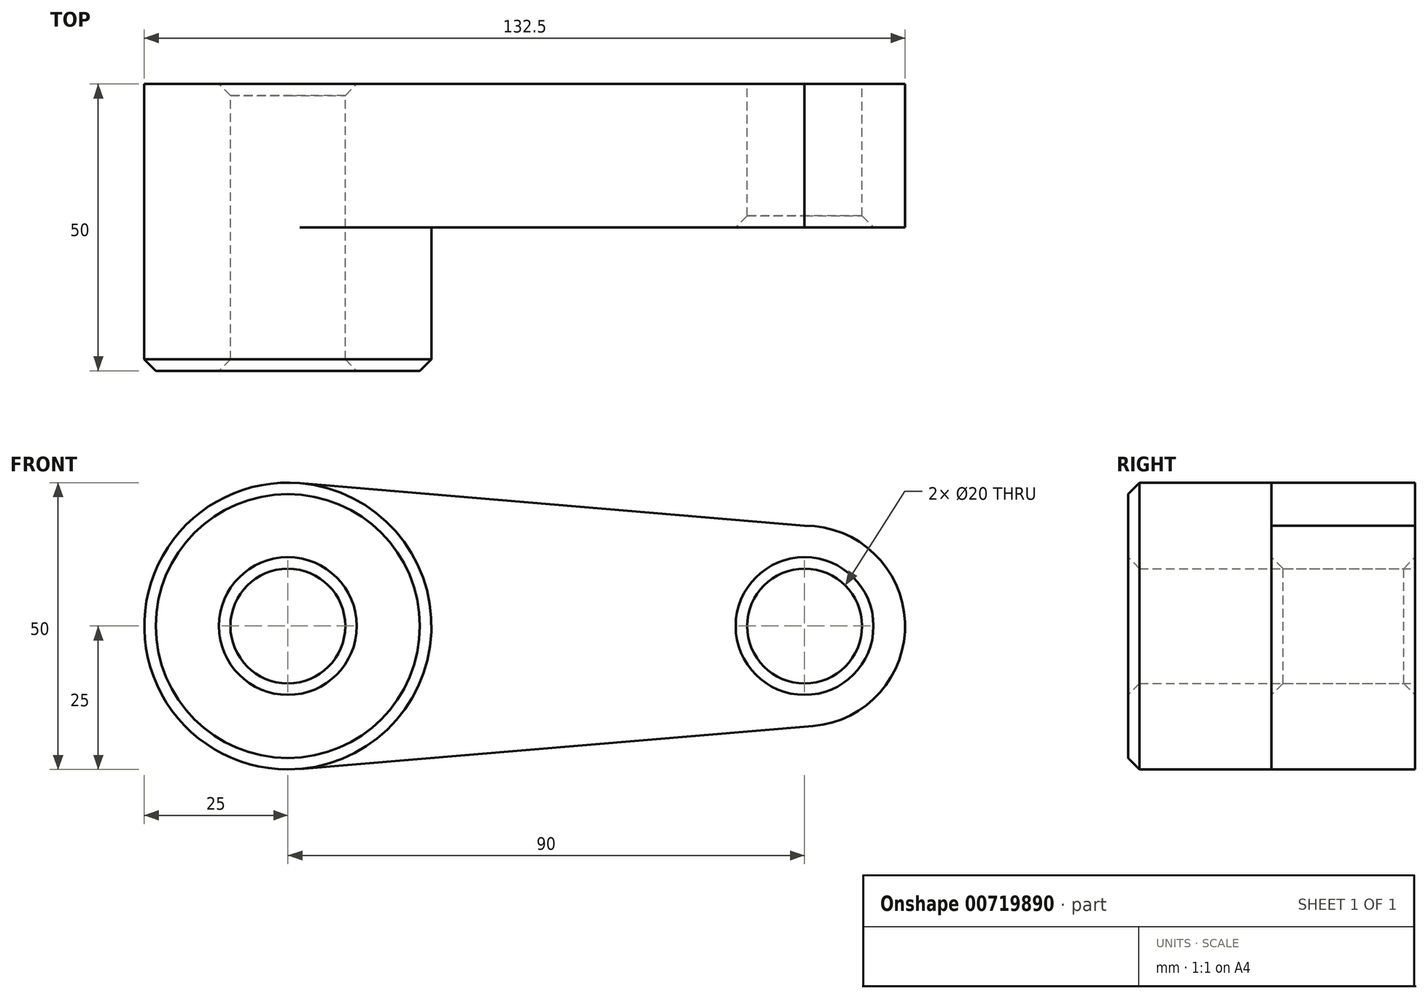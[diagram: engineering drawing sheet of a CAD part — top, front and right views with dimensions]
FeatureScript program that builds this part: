
annotation { "Feature Type Name" : "Feature", "Feature Type Description" : "" }
export const myFeature = defineFeature(function(context is Context, id is Id, definition is map)
    precondition{}
    {
        {
            var Q0;
            Q0=qCreatedBy(makeId("Front.planeOp"),FACE);
            var sketch = newSketch(context, id + "F0", { "sketchPlane" : qUnion([Q0])});
            skCircle(sketch, "E0", {"center": v(0, 0) * mm, "radius": 25 * mm});
            skCircle(sketch, "E1", {"center": v(90, 0) * mm, "radius": 17.5 * mm});
            skLineSegment(sketch, "E2", {"start": v(2.1, 24.91) * mm, "end": v(90, 17.5) * mm});
            skLineSegment(sketch, "E3", {"start": v(2.08, -24.91) * mm, "end": v(91.46, -17.44) * mm});
            skCircle(sketch, "E4", {"center": v(90, 0) * mm, "radius": 10 * mm});
            skCircle(sketch, "E5", {"center": v(0, 0) * mm, "radius": 10 * mm});
            skSolve(sketch);
        }
        {
            var Q0;
            Q0 = qSketchRegion(id + "F0", true);
            extrude(context, id + "F1", {"entities" : qUnion([Q0]), "depth" : 25 * mm, "offsetDistance" : 25 * mm});
        }
        {
            var Q0;
            Q0=makeQuery(id+"F0.imprint","IMPRINT",FACE,{"disambiguationData":[TD([[makeQuery(id+"F0.imprint","IMPRINT",EDGE,{"derivedFrom":sQuery(id+"F0.wireOp",EDGE,"E5")}),-1.0]])]});
            extrude(context, id + "F2", {"entities" : qUnion([Q0]), "operationType" : NewBodyOperationType.ADD, "depth" : 50 * mm, "offsetDistance" : 25 * mm});
        }
        {
            var Q0;
            {var subQ0=sQuery(id+"F0.wireOp",EDGE,"E5");Q0=makeQuery(id+"F2.boolean.opBoolean","MERGE",FACE,{"derivedFrom":[makeQuery(id+"F1.opExtrude","SWEPT_FACE",FACE,{"disambiguationData":[OSD([subQ0])]}),makeQuery(id+"F2.opExtrude","SWEPT_FACE",FACE,{"disambiguationData":[OSD([subQ0])]})]});}
            var Q1;
            Q1=makeQuery(id+"F2.opExtrude","CAP_EDGE",EDGE,{"disambiguationData":[OSD([sQuery(id+"F0.wireOp",EDGE,"E0")])],"isStart":false});
            var Q2;
            Q2=makeQuery(id+"F1.opExtrude","CAP_EDGE",EDGE,{"disambiguationData":[OSD([sQuery(id+"F0.wireOp",EDGE,"E4")])],"isStart":false});
            chamfer(context, id + "F3", {"entities" : qUnion([Q0, Q1, Q2]), "width" : 2 * mm, "tangentPropagation" : true});
        }
    });
